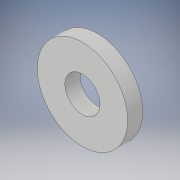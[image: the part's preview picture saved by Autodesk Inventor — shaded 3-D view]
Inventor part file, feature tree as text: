
AUTODESK INVENTOR PART (.ipt)
format: ipt  version: 2019 (Build 230136000, 136)  size: 190,464 bytes
history: native  units: mm
features: extrude x1, sketch x1
ambient origin geometry x8: Origin, YZ Plane, XZ Plane, XY Plane, X Axis, Y Axis, Z Axis, Center Point
bodies: Solid1 (feature_tree)
feature tree (2):
  extrude  "Extrusion1"  Depth=1.5mm
  sketch  "Sketch1"  dims[d0=3.5mm d1=9.0mm d2=1.5mm d3=0.0mm]
